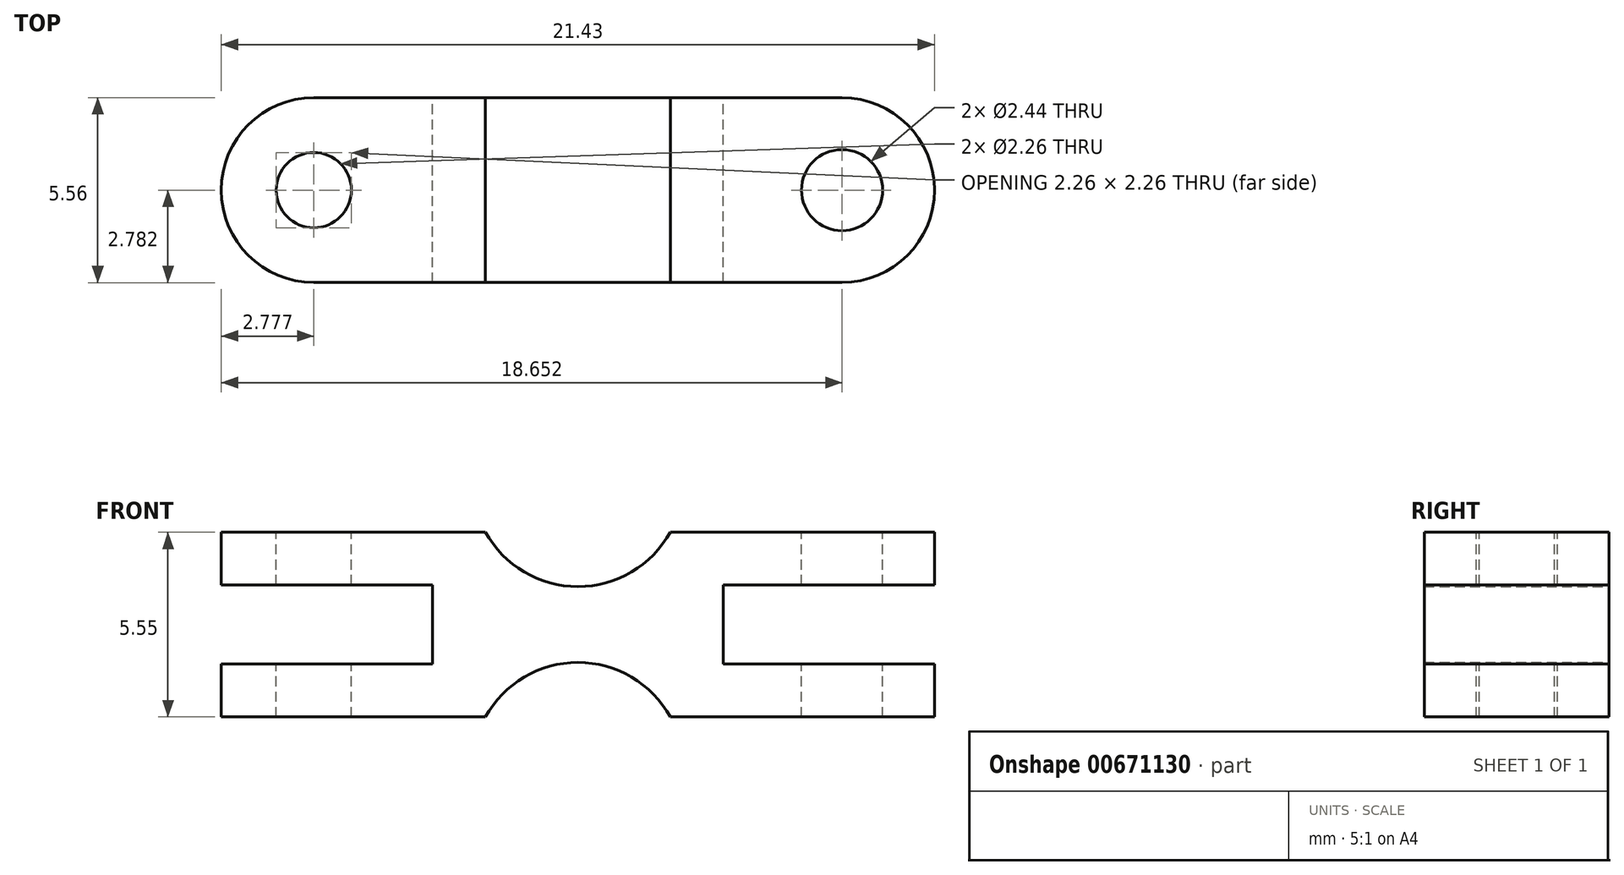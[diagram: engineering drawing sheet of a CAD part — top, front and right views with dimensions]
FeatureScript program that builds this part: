
annotation { "Feature Type Name" : "Feature", "Feature Type Description" : "" }
export const myFeature = defineFeature(function(context is Context, id is Id, definition is map)
    precondition{}
    {
        {
            var Q0;
            Q0=qCreatedBy(makeId("Front.planeOp"),FACE);
            var sketch = newSketch(context, id + "F0", { "sketchPlane" : qUnion([Q0])});
            skLineSegment(sketch, "E0", {"start": v(19.5, 28.35) * mm, "end": v(27.45, 28.35) * mm});
            skLineSegment(sketch, "E1", {"start": v(27.45, 28.35) * mm, "end": v(27.45, 22.8) * mm});
            skLineSegment(sketch, "E2", {"start": v(27.45, 22.8) * mm, "end": v(19.5, 22.8) * mm});
            skLineSegment(sketch, "E3", {"start": v(19.5, 22.8) * mm, "end": v(19.5, 24.39) * mm});
            skLineSegment(sketch, "E4", {"start": v(19.5, 24.39) * mm, "end": v(25.86, 24.39) * mm});
            skLineSegment(sketch, "E5", {"start": v(25.86, 24.39) * mm, "end": v(25.86, 26.77) * mm});
            skLineSegment(sketch, "E6", {"start": v(25.86, 26.77) * mm, "end": v(19.5, 26.77) * mm});
            skLineSegment(sketch, "E7", {"start": v(19.5, 26.77) * mm, "end": v(19.5, 28.35) * mm});
            skArc(sketch, "E8", {"start": v(27.45, 28.35) * mm, "mid": v(30.22, 26.72) * mm, "end": v(33, 28.35) * mm});
            skArc(sketch, "E9", {"start": v(33, 22.8) * mm, "mid": v(30.22, 24.44) * mm, "end": v(27.45, 22.8) * mm});
            skLineSegment(sketch, "E10", {"start": v(33, 28.35) * mm, "end": v(33, 22.8) * mm});
            skLineSegment(sketch, "E11", {"start": v(33, 22.8) * mm, "end": v(40.94, 22.8) * mm});
            skLineSegment(sketch, "E12", {"start": v(40.94, 22.8) * mm, "end": v(40.94, 24.39) * mm});
            skLineSegment(sketch, "E13", {"start": v(34.59, 24.39) * mm, "end": v(34.59, 26.77) * mm});
            skLineSegment(sketch, "E14", {"start": v(34.59, 26.77) * mm, "end": v(40.94, 26.77) * mm});
            skLineSegment(sketch, "E15", {"start": v(40.94, 26.77) * mm, "end": v(40.94, 28.35) * mm});
            skLineSegment(sketch, "E16", {"start": v(40.94, 28.35) * mm, "end": v(33, 28.35) * mm});
            skLineSegment(sketch, "E17", {"start": v(34.59, 24.39) * mm, "end": v(40.94, 24.39) * mm});
            skSolve(sketch);
        }
        {
            var Q0;
            Q0=qSketchRegion(id+"F0",true);
            extrude(context, id + "F1", {"entities" : qUnion([Q0]), "depth" : 5.56 * mm});
        }
        {
            var Q0;
            Q0=makeQuery(id+"F1.opExtrude","SWEPT_FACE",FACE,{"disambiguationData":[OSD([sQuery(id+"F0.wireOp",EDGE,"E0")])]});
            var sketch = newSketch(context, id + "F2", { "sketchPlane" : qUnion([Q0])});
            skCircle(sketch, "E18", {"center": v(22.29, -2.78) * mm, "radius": 1.13 * mm});
            skCircle(sketch, "E19", {"center": v(38.16, -2.78) * mm, "radius": 1.22 * mm});
            skSolve(sketch);
        }
        {
            var Q0;
            Q0=qSketchRegion(id+"F2",true);
            extrude(context, id + "F3", {"entities" : qUnion([Q0]), "operationType" : NewBodyOperationType.REMOVE, "oppositeDirection" : true, "depth" : 25.4 * mm});
        }
        {
            var Q0;
            Q0=makeQuery(id+"F1.opExtrude","CAP_EDGE",EDGE,{"disambiguationData":[OSD([sQuery(id+"F0.wireOp",EDGE,"E3")])],"isStart":true});
            var Q1;
            Q1=makeQuery(id+"F1.opExtrude","CAP_EDGE",EDGE,{"disambiguationData":[OSD([sQuery(id+"F0.wireOp",EDGE,"E7")])],"isStart":true});
            var Q2;
            Q2=makeQuery(id+"F1.opExtrude","CAP_EDGE",EDGE,{"disambiguationData":[OSD([sQuery(id+"F0.wireOp",EDGE,"E7")])],"isStart":false});
            var Q3;
            Q3=makeQuery(id+"F1.opExtrude","CAP_EDGE",EDGE,{"disambiguationData":[OSD([sQuery(id+"F0.wireOp",EDGE,"E3")])],"isStart":false});
            var Q4;
            Q4=makeQuery(id+"F1.opExtrude","CAP_EDGE",EDGE,{"disambiguationData":[OSD([sQuery(id+"F0.wireOp",EDGE,"E12")])],"isStart":true});
            var Q5;
            Q5=makeQuery(id+"F1.opExtrude","CAP_EDGE",EDGE,{"disambiguationData":[OSD([sQuery(id+"F0.wireOp",EDGE,"E15")])],"isStart":true});
            var Q6;
            Q6=makeQuery(id+"F1.opExtrude","CAP_EDGE",EDGE,{"disambiguationData":[OSD([sQuery(id+"F0.wireOp",EDGE,"E12")])],"isStart":false});
            var Q7;
            Q7=makeQuery(id+"F1.opExtrude","CAP_EDGE",EDGE,{"disambiguationData":[OSD([sQuery(id+"F0.wireOp",EDGE,"E15")])],"isStart":false});
            fillet(context, id + "F4", {"entities" : qUnion([Q0, Q1, Q2, Q3, Q4, Q5, Q6, Q7]), "radius" : 2.78 * mm, "tangentPropagation" : true, "allowEdgeOverflow" : false});
        }
    });
